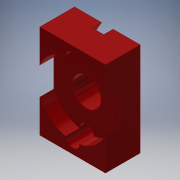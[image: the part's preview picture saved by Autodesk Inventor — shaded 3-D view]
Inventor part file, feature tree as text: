
AUTODESK INVENTOR PART (.ipt)
format: ipt  version: 2019 (Build 230136000, 136)  size: 185,344 bytes
history: native  units: mm
features: extrude x5, sketch x5, reference x5, other x5, pattern_circular x1, mirror x1, projected_geometry x1
ambient origin geometry x8: Origin, YZ Plane, XZ Plane, XY Plane, X Axis, Y Axis, Z Axis, Center Point
bodies: Solid1 (feature_tree)
feature tree (23):
  extrude  "Extrusion1"  Depth=14.0mm
  extrude  "Extrusion2"  Depth=4.4mm TaperAngle=0.0deg
  extrude  "Extrusion4"  Depth=3.0mm TaperAngle=0.0deg
  extrude  "Extrusion3"  Depth=2.0mm TaperAngle=0.0deg
  extrude  "Extrusion5"  Depth=3.0mm TaperAngle=0.0deg
  pattern_circular  "Circular Pattern1"  [2 undecoded]
  mirror  "Mirror1"
  sketch  "Sketch1"  dims[d0=20.0mm d1=14.0mm]
  sketch  "Sketch2"  dims[d2=6.1mm d3=4.4mm d4=0.0mm]
  reference  "Reference1"
  projected_geometry  "Projected Loop1"
  sketch  "Sketch3"  dims[d5=15.2mm d6=3.0mm d7=0.0mm]
  reference  "Reference2"
  reference  "Reference3"
  sketch  "Sketch4"  dims[d8=4.77mm d9=2.0mm d10=0.0mm]
  reference  "Reference4"
  reference  "Reference5"
  sketch  "Sketch5"  dims[d11=3.0mm d12=5.0mm d13=0.0mm d15=0.62mm d16=0.366606mm d17=3.0mm d18=0.0mm d19=40.0mm d20=180.0deg]
  parser-record x1  (decoder bookkeeping rows leaked as tree rows — omitted from the tree; the rows remain in map.json)
  other  "Kinematics.iam"
  other  "Motor-GM15BY:2"
  other  "Motor-Body:1"
  other  "Mini-Q Ball caster:1"
note: 2 required parameter values undecoded (feature->parameter linkage not recoverable at this tier; creation-order binding heuristic only, values carry confidence <= 0.55)
note: 1 file-system path scrubbed to <path> (originals preserved in map.json)
